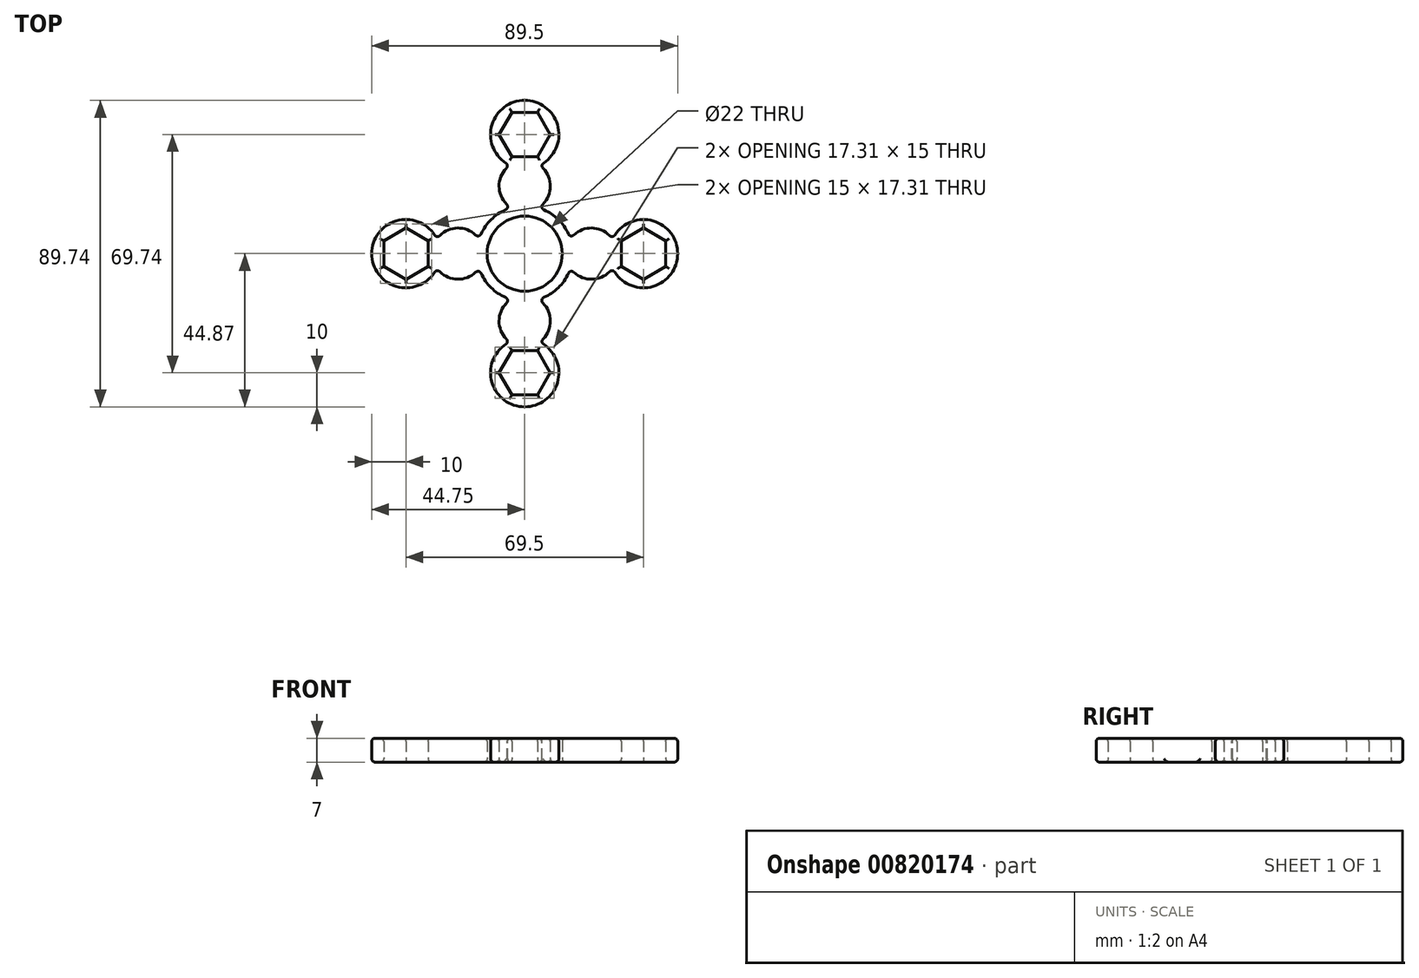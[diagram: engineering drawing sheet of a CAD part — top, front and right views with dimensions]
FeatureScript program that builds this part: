
annotation { "Feature Type Name" : "Feature", "Feature Type Description" : "" }
export const myFeature = defineFeature(function(context is Context, id is Id, definition is map)
    precondition{}
    {
        {
            var Q0;
            Q0=qCreatedBy(makeId("Top.planeOp"),FACE);
            var sketch = newSketch(context, id + "F0", { "sketchPlane" : qUnion([Q0])});
            skCircle(sketch, "E0", {"center": v(0, 0) * mm, "radius": 11 * mm});
            skCircle(sketch, "E1", {"center": v(0, 0) * mm, "radius": 14 * mm});
            skCircle(sketch, "E2", {"center": v(19.5, 0) * mm, "radius": 7.5 * mm});
            skCircle(sketch, "E3.MirrorC", {"center": v(-19.5, 0) * mm, "radius": 7.5 * mm});
            skCircle(sketch, "E4", {"center": v(0, 19.76) * mm, "radius": 7.5 * mm});
            skCircle(sketch, "E5.MirrorC", {"center": v(0, -19.76) * mm, "radius": 7.5 * mm});
            skCircle(sketch, "E6", {"center": v(34.75, 0) * mm, "radius": 10 * mm});
            skCircle(sketch, "E7.MirrorC", {"center": v(-34.75, 0) * mm, "radius": 10 * mm});
            skCircle(sketch, "E8", {"center": v(0, 34.87) * mm, "radius": 10 * mm});
            skCircle(sketch, "E9.MirrorC", {"center": v(0, -34.87) * mm, "radius": 10 * mm});
            skCircle(sketch, "E10.cCircle", {"center": v(34.75, 0) * mm, "radius": 6.5 * mm, "construction": true});
            skLineSegment(sketch, "E10.0", {"start": v(28.25, -3.75) * mm, "end": v(28.25, 3.75) * mm});
            skLineSegment(sketch, "E10.1", {"start": v(28.25, 3.75) * mm, "end": v(34.75, 7.5) * mm});
            skLineSegment(sketch, "E10.2", {"start": v(34.75, 7.5) * mm, "end": v(41.25, 3.75) * mm});
            skLineSegment(sketch, "E10.3", {"start": v(41.25, 3.75) * mm, "end": v(41.25, -3.75) * mm});
            skLineSegment(sketch, "E10.4", {"start": v(41.25, -3.75) * mm, "end": v(34.75, -7.5) * mm});
            skLineSegment(sketch, "E10.5", {"start": v(34.75, -7.5) * mm, "end": v(28.25, -3.75) * mm});
            skPoint(sketch, "E10.0.midPoint", {"position": v(28.25, 0) * mm});
            skCircle(sketch, "E11.cCircle", {"center": v(0, 34.87) * mm, "radius": 6.5 * mm, "construction": true});
            skLineSegment(sketch, "E11.0", {"start": v(3.75, 28.37) * mm, "end": v(-3.75, 28.37) * mm});
            skLineSegment(sketch, "E11.1", {"start": v(-3.75, 28.37) * mm, "end": v(-7.5, 34.87) * mm});
            skLineSegment(sketch, "E11.2", {"start": v(-7.5, 34.87) * mm, "end": v(-3.75, 41.37) * mm});
            skLineSegment(sketch, "E11.3", {"start": v(-3.75, 41.37) * mm, "end": v(3.75, 41.37) * mm});
            skLineSegment(sketch, "E11.4", {"start": v(3.75, 41.37) * mm, "end": v(7.5, 34.87) * mm});
            skLineSegment(sketch, "E11.5", {"start": v(7.5, 34.87) * mm, "end": v(3.75, 28.37) * mm});
            skPoint(sketch, "E11.0.midPoint", {"position": v(0, 28.37) * mm});
            skCircle(sketch, "E12.MirrorC", {"center": v(-34.75, 0) * mm, "radius": 6.5 * mm, "construction": true});
            skLineSegment(sketch, "E13.MirrorCS", {"start": v(-34.75, 7.5) * mm, "end": v(-41.25, 3.75) * mm});
            skLineSegment(sketch, "E14.MirrorCS", {"start": v(-41.25, -3.75) * mm, "end": v(-34.75, -7.5) * mm});
            skLineSegment(sketch, "E15.MirrorCS", {"start": v(-34.75, -7.5) * mm, "end": v(-28.25, -3.75) * mm});
            skLineSegment(sketch, "E16.MirrorCS", {"start": v(-28.25, -3.75) * mm, "end": v(-28.25, 3.75) * mm});
            skLineSegment(sketch, "E17.MirrorCS", {"start": v(-28.25, 3.75) * mm, "end": v(-34.75, 7.5) * mm});
            skLineSegment(sketch, "E18.MirrorCS", {"start": v(-41.25, 3.75) * mm, "end": v(-41.25, -3.75) * mm});
            skCircle(sketch, "E19.MirrorC", {"center": v(0, -34.87) * mm, "radius": 6.5 * mm, "construction": true});
            skLineSegment(sketch, "E20.MirrorCS", {"start": v(7.5, -34.87) * mm, "end": v(3.75, -28.37) * mm});
            skLineSegment(sketch, "E21.MirrorCS", {"start": v(3.75, -41.37) * mm, "end": v(7.5, -34.87) * mm});
            skLineSegment(sketch, "E22.MirrorCS", {"start": v(-3.75, -41.37) * mm, "end": v(3.75, -41.37) * mm});
            skLineSegment(sketch, "E23.MirrorCS", {"start": v(-7.5, -34.87) * mm, "end": v(-3.75, -41.37) * mm});
            skLineSegment(sketch, "E24.MirrorCS", {"start": v(-3.75, -28.37) * mm, "end": v(-7.5, -34.87) * mm});
            skLineSegment(sketch, "E25.MirrorCS", {"start": v(3.75, -28.37) * mm, "end": v(-3.75, -28.37) * mm});
            skSolve(sketch);
        }
        {
            var Q0;
            Q0 = qSketchRegion(id + "F0", true);
            extrude(context, id + "F1", {"entities" : qUnion([Q0]), "depth" : 7 * mm, "offsetDistance" : 25 * mm});
        }
        {
            var Q0;
            Q0=makeQuery(id+"F1.opExtrude","CAP_EDGE",EDGE,{"disambiguationData":[OSD([sQuery(id+"F0.wireOp",EDGE,"E0")])],"isStart":true});
            var Q1;
            {var subQ0=sQuery(id+"F0.wireOp",EDGE,"E1");Q1=makeQuery(id+"F1.opExtrude","CAP_EDGE",EDGE,{"disambiguationData":[OSD([subQ0]),TDD([makeQuery(id+"F0.imprint","IMPRINT",EDGE,{"disambiguationData":[TD([[makeQuery(id+"F0.imprint","INTERSECT",VERTEX,{"disambiguationData":[OD(1.0)],"derivedFrom":[subQ0,sQuery(id+"F0.wireOp",EDGE,"E5.MirrorC")]}),-1.0]])],"derivedFrom":subQ0})])],"isStart":true});}
            var Q2;
            {var subQ0=sQuery(id+"F0.wireOp",EDGE,"E1");Q2=makeQuery(id+"F1.opExtrude","CAP_EDGE",EDGE,{"disambiguationData":[OSD([subQ0]),TDD([makeQuery(id+"F0.imprint","IMPRINT",EDGE,{"disambiguationData":[TD([[makeQuery(id+"F0.imprint","INTERSECT",VERTEX,{"disambiguationData":[OD(1.0)],"derivedFrom":[subQ0,sQuery(id+"F0.wireOp",EDGE,"E3.MirrorC")]}),-1.0]])],"derivedFrom":subQ0})])],"isStart":true});}
            var Q3;
            {var subQ0=sQuery(id+"F0.wireOp",EDGE,"E1");Q3=makeQuery(id+"F1.opExtrude","CAP_EDGE",EDGE,{"disambiguationData":[OSD([subQ0]),TDD([makeQuery(id+"F0.imprint","IMPRINT",EDGE,{"disambiguationData":[TD([[makeQuery(id+"F0.imprint","INTERSECT",VERTEX,{"disambiguationData":[OD(1.0)],"derivedFrom":[subQ0,sQuery(id+"F0.wireOp",EDGE,"E4")]}),-1.0]])],"derivedFrom":subQ0})])],"isStart":true});}
            var Q4;
            {var subQ0=sQuery(id+"F0.wireOp",EDGE,"E1");Q4=makeQuery(id+"F1.opExtrude","CAP_EDGE",EDGE,{"disambiguationData":[OSD([subQ0]),TDD([makeQuery(id+"F0.imprint","IMPRINT",EDGE,{"disambiguationData":[TD([[makeQuery(id+"F0.imprint","INTERSECT",VERTEX,{"disambiguationData":[OD(0.0)],"derivedFrom":[subQ0,sQuery(id+"F0.wireOp",EDGE,"E4")]}),1.0]])],"derivedFrom":subQ0})])],"isStart":true});}
            var Q5;
            Q5=makeQuery(id+"F1.opExtrude","CAP_EDGE",EDGE,{"disambiguationData":[OSD([sQuery(id+"F0.wireOp",EDGE,"E13.MirrorCS")])],"isStart":true});
            var Q6;
            Q6=makeQuery(id+"F1.opExtrude","CAP_EDGE",EDGE,{"disambiguationData":[OSD([sQuery(id+"F0.wireOp",EDGE,"E17.MirrorCS")])],"isStart":true});
            var Q7;
            Q7=makeQuery(id+"F1.opExtrude","CAP_EDGE",EDGE,{"disambiguationData":[OSD([sQuery(id+"F0.wireOp",EDGE,"E16.MirrorCS")])],"isStart":true});
            var Q8;
            Q8=makeQuery(id+"F1.opExtrude","CAP_EDGE",EDGE,{"disambiguationData":[OSD([sQuery(id+"F0.wireOp",EDGE,"E15.MirrorCS")])],"isStart":true});
            var Q9;
            Q9=makeQuery(id+"F1.opExtrude","CAP_EDGE",EDGE,{"disambiguationData":[OSD([sQuery(id+"F0.wireOp",EDGE,"E14.MirrorCS")])],"isStart":true});
            var Q10;
            Q10=makeQuery(id+"F1.opExtrude","CAP_EDGE",EDGE,{"disambiguationData":[OSD([sQuery(id+"F0.wireOp",EDGE,"E18.MirrorCS")])],"isStart":true});
            var Q11;
            Q11=makeQuery(id+"F1.opExtrude","CAP_EDGE",EDGE,{"disambiguationData":[OSD([sQuery(id+"F0.wireOp",EDGE,"E10.4")])],"isStart":true});
            var Q12;
            Q12=makeQuery(id+"F1.opExtrude","CAP_EDGE",EDGE,{"disambiguationData":[OSD([sQuery(id+"F0.wireOp",EDGE,"E10.5")])],"isStart":true});
            var Q13;
            Q13=makeQuery(id+"F1.opExtrude","CAP_EDGE",EDGE,{"disambiguationData":[OSD([sQuery(id+"F0.wireOp",EDGE,"E10.0")])],"isStart":true});
            var Q14;
            Q14=makeQuery(id+"F1.opExtrude","CAP_EDGE",EDGE,{"disambiguationData":[OSD([sQuery(id+"F0.wireOp",EDGE,"E10.1")])],"isStart":true});
            var Q15;
            Q15=makeQuery(id+"F1.opExtrude","CAP_EDGE",EDGE,{"disambiguationData":[OSD([sQuery(id+"F0.wireOp",EDGE,"E10.2")])],"isStart":true});
            var Q16;
            Q16=makeQuery(id+"F1.opExtrude","CAP_EDGE",EDGE,{"disambiguationData":[OSD([sQuery(id+"F0.wireOp",EDGE,"E10.3")])],"isStart":true});
            var Q17;
            Q17=makeQuery(id+"F1.opExtrude","CAP_EDGE",EDGE,{"disambiguationData":[OSD([sQuery(id+"F0.wireOp",EDGE,"E25.MirrorCS")])],"isStart":true});
            var Q18;
            Q18=makeQuery(id+"F1.opExtrude","CAP_EDGE",EDGE,{"disambiguationData":[OSD([sQuery(id+"F0.wireOp",EDGE,"E24.MirrorCS")])],"isStart":true});
            var Q19;
            Q19=makeQuery(id+"F1.opExtrude","CAP_EDGE",EDGE,{"disambiguationData":[OSD([sQuery(id+"F0.wireOp",EDGE,"E23.MirrorCS")])],"isStart":true});
            var Q20;
            Q20=makeQuery(id+"F1.opExtrude","CAP_EDGE",EDGE,{"disambiguationData":[OSD([sQuery(id+"F0.wireOp",EDGE,"E22.MirrorCS")])],"isStart":true});
            var Q21;
            Q21=makeQuery(id+"F1.opExtrude","CAP_EDGE",EDGE,{"disambiguationData":[OSD([sQuery(id+"F0.wireOp",EDGE,"E21.MirrorCS")])],"isStart":true});
            var Q22;
            Q22=makeQuery(id+"F1.opExtrude","CAP_EDGE",EDGE,{"disambiguationData":[OSD([sQuery(id+"F0.wireOp",EDGE,"E20.MirrorCS")])],"isStart":true});
            var Q23;
            Q23=makeQuery(id+"F1.opExtrude","CAP_EDGE",EDGE,{"disambiguationData":[OSD([sQuery(id+"F0.wireOp",EDGE,"E11.1")])],"isStart":true});
            var Q24;
            Q24=makeQuery(id+"F1.opExtrude","CAP_EDGE",EDGE,{"disambiguationData":[OSD([sQuery(id+"F0.wireOp",EDGE,"E11.2")])],"isStart":true});
            var Q25;
            Q25=makeQuery(id+"F1.opExtrude","CAP_EDGE",EDGE,{"disambiguationData":[OSD([sQuery(id+"F0.wireOp",EDGE,"E11.3")])],"isStart":true});
            var Q26;
            Q26=makeQuery(id+"F1.opExtrude","CAP_EDGE",EDGE,{"disambiguationData":[OSD([sQuery(id+"F0.wireOp",EDGE,"E11.4")])],"isStart":true});
            var Q27;
            Q27=makeQuery(id+"F1.opExtrude","CAP_EDGE",EDGE,{"disambiguationData":[OSD([sQuery(id+"F0.wireOp",EDGE,"E11.5")])],"isStart":true});
            var Q28;
            Q28=makeQuery(id+"F1.opExtrude","CAP_EDGE",EDGE,{"disambiguationData":[OSD([sQuery(id+"F0.wireOp",EDGE,"E11.0")])],"isStart":true});
            var Q29;
            {var subQ0=sQuery(id+"F0.wireOp",EDGE,"E4");Q29=makeQuery(id+"F1.opExtrude","SWEPT_FACE",FACE,{"disambiguationData":[OSD([subQ0]),TDD([makeQuery(id+"F0.imprint","IMPRINT",EDGE,{"disambiguationData":[TD([[makeQuery(id+"F0.imprint","INTERSECT",VERTEX,{"disambiguationData":[OD(1.0)],"derivedFrom":[sQuery(id+"F0.wireOp",EDGE,"E1"),subQ0]}),1.0]])],"derivedFrom":subQ0})])]});}
            var Q30;
            Q30=makeQuery(id+"F1.opExtrude","SWEPT_FACE",FACE,{"disambiguationData":[OSD([sQuery(id+"F0.wireOp",EDGE,"E8")])]});
            var Q31;
            {var subQ0=sQuery(id+"F0.wireOp",EDGE,"E4");Q31=makeQuery(id+"F1.opExtrude","SWEPT_FACE",FACE,{"disambiguationData":[OSD([subQ0]),TDD([makeQuery(id+"F0.imprint","IMPRINT",EDGE,{"disambiguationData":[TD([[makeQuery(id+"F0.imprint","INTERSECT",VERTEX,{"disambiguationData":[OD(0.0)],"derivedFrom":[sQuery(id+"F0.wireOp",EDGE,"E1"),subQ0]}),-1.0]])],"derivedFrom":subQ0})])]});}
            var Q32;
            {var subQ0=sQuery(id+"F0.wireOp",EDGE,"E1");Q32=makeQuery(id+"F1.opExtrude","SWEPT_FACE",FACE,{"disambiguationData":[OSD([subQ0]),TDD([makeQuery(id+"F0.imprint","IMPRINT",EDGE,{"disambiguationData":[TD([[makeQuery(id+"F0.imprint","INTERSECT",VERTEX,{"disambiguationData":[OD(0.0)],"derivedFrom":[subQ0,sQuery(id+"F0.wireOp",EDGE,"E4")]}),1.0]])],"derivedFrom":subQ0})])]});}
            var Q33;
            {var subQ0=sQuery(id+"F0.wireOp",EDGE,"E2");Q33=makeQuery(id+"F1.opExtrude","SWEPT_FACE",FACE,{"disambiguationData":[OSD([subQ0]),TDD([makeQuery(id+"F0.imprint","IMPRINT",EDGE,{"disambiguationData":[TD([[makeQuery(id+"F0.imprint","INTERSECT",VERTEX,{"disambiguationData":[OD(0.0)],"derivedFrom":[sQuery(id+"F0.wireOp",EDGE,"E1"),subQ0]}),1.0]])],"derivedFrom":subQ0})])]});}
            var Q34;
            Q34=makeQuery(id+"F1.opExtrude","SWEPT_FACE",FACE,{"disambiguationData":[OSD([sQuery(id+"F0.wireOp",EDGE,"E6")])]});
            var Q35;
            {var subQ0=sQuery(id+"F0.wireOp",EDGE,"E2");Q35=makeQuery(id+"F1.opExtrude","SWEPT_FACE",FACE,{"disambiguationData":[OSD([subQ0]),TDD([makeQuery(id+"F0.imprint","IMPRINT",EDGE,{"disambiguationData":[TD([[makeQuery(id+"F0.imprint","INTERSECT",VERTEX,{"disambiguationData":[OD(1.0)],"derivedFrom":[sQuery(id+"F0.wireOp",EDGE,"E1"),subQ0]}),-1.0]])],"derivedFrom":subQ0})])]});}
            var Q36;
            {var subQ0=sQuery(id+"F0.wireOp",EDGE,"E1");Q36=makeQuery(id+"F1.opExtrude","SWEPT_FACE",FACE,{"disambiguationData":[OSD([subQ0]),TDD([makeQuery(id+"F0.imprint","IMPRINT",EDGE,{"disambiguationData":[TD([[makeQuery(id+"F0.imprint","INTERSECT",VERTEX,{"disambiguationData":[OD(1.0)],"derivedFrom":[subQ0,sQuery(id+"F0.wireOp",EDGE,"E5.MirrorC")]}),-1.0]])],"derivedFrom":subQ0})])]});}
            var Q37;
            {var subQ0=sQuery(id+"F0.wireOp",EDGE,"E5.MirrorC");Q37=makeQuery(id+"F1.opExtrude","SWEPT_FACE",FACE,{"disambiguationData":[OSD([subQ0]),TDD([makeQuery(id+"F0.imprint","IMPRINT",EDGE,{"disambiguationData":[TD([[makeQuery(id+"F0.imprint","INTERSECT",VERTEX,{"disambiguationData":[OD(1.0)],"derivedFrom":[sQuery(id+"F0.wireOp",EDGE,"E1"),subQ0]}),-1.0]])],"derivedFrom":subQ0})])]});}
            var Q38;
            Q38=makeQuery(id+"F1.opExtrude","SWEPT_FACE",FACE,{"disambiguationData":[OSD([sQuery(id+"F0.wireOp",EDGE,"E9.MirrorC")])]});
            var Q39;
            {var subQ0=sQuery(id+"F0.wireOp",EDGE,"E1");Q39=makeQuery(id+"F1.opExtrude","SWEPT_FACE",FACE,{"disambiguationData":[OSD([subQ0]),TDD([makeQuery(id+"F0.imprint","IMPRINT",EDGE,{"disambiguationData":[TD([[makeQuery(id+"F0.imprint","INTERSECT",VERTEX,{"disambiguationData":[OD(1.0)],"derivedFrom":[subQ0,sQuery(id+"F0.wireOp",EDGE,"E3.MirrorC")]}),-1.0]])],"derivedFrom":subQ0})])]});}
            var Q40;
            {var subQ0=sQuery(id+"F0.wireOp",EDGE,"E5.MirrorC");Q40=makeQuery(id+"F1.opExtrude","SWEPT_FACE",FACE,{"disambiguationData":[OSD([subQ0]),TDD([makeQuery(id+"F0.imprint","IMPRINT",EDGE,{"disambiguationData":[TD([[makeQuery(id+"F0.imprint","INTERSECT",VERTEX,{"disambiguationData":[OD(0.0)],"derivedFrom":[sQuery(id+"F0.wireOp",EDGE,"E1"),subQ0]}),1.0]])],"derivedFrom":subQ0})])]});}
            var Q41;
            {var subQ0=sQuery(id+"F0.wireOp",EDGE,"E3.MirrorC");Q41=makeQuery(id+"F1.opExtrude","SWEPT_FACE",FACE,{"disambiguationData":[OSD([subQ0]),TDD([makeQuery(id+"F0.imprint","IMPRINT",EDGE,{"disambiguationData":[TD([[makeQuery(id+"F0.imprint","INTERSECT",VERTEX,{"disambiguationData":[OD(1.0)],"derivedFrom":[sQuery(id+"F0.wireOp",EDGE,"E1"),subQ0]}),1.0]])],"derivedFrom":subQ0})])]});}
            var Q42;
            Q42=makeQuery(id+"F1.opExtrude","SWEPT_FACE",FACE,{"disambiguationData":[OSD([sQuery(id+"F0.wireOp",EDGE,"E7.MirrorC")])]});
            var Q43;
            {var subQ0=sQuery(id+"F0.wireOp",EDGE,"E1");Q43=makeQuery(id+"F1.opExtrude","SWEPT_FACE",FACE,{"disambiguationData":[OSD([subQ0]),TDD([makeQuery(id+"F0.imprint","IMPRINT",EDGE,{"disambiguationData":[TD([[makeQuery(id+"F0.imprint","INTERSECT",VERTEX,{"disambiguationData":[OD(1.0)],"derivedFrom":[subQ0,sQuery(id+"F0.wireOp",EDGE,"E4")]}),-1.0]])],"derivedFrom":subQ0})])]});}
            var Q44;
            {var subQ0=sQuery(id+"F0.wireOp",EDGE,"E3.MirrorC");Q44=makeQuery(id+"F1.opExtrude","SWEPT_FACE",FACE,{"disambiguationData":[OSD([subQ0]),TDD([makeQuery(id+"F0.imprint","IMPRINT",EDGE,{"disambiguationData":[TD([[makeQuery(id+"F0.imprint","INTERSECT",VERTEX,{"disambiguationData":[OD(0.0)],"derivedFrom":[sQuery(id+"F0.wireOp",EDGE,"E1"),subQ0]}),-1.0]])],"derivedFrom":subQ0})])]});}
            var Q45;
            Q45=makeQuery(id+"F1.opExtrude","CAP_EDGE",EDGE,{"disambiguationData":[OSD([sQuery(id+"F0.wireOp",EDGE,"E14.MirrorCS")])],"isStart":false});
            var Q46;
            Q46=makeQuery(id+"F1.opExtrude","CAP_EDGE",EDGE,{"disambiguationData":[OSD([sQuery(id+"F0.wireOp",EDGE,"E13.MirrorCS")])],"isStart":false});
            var Q47;
            Q47=makeQuery(id+"F1.opExtrude","CAP_EDGE",EDGE,{"disambiguationData":[OSD([sQuery(id+"F0.wireOp",EDGE,"E17.MirrorCS")])],"isStart":false});
            var Q48;
            Q48=makeQuery(id+"F1.opExtrude","CAP_EDGE",EDGE,{"disambiguationData":[OSD([sQuery(id+"F0.wireOp",EDGE,"E16.MirrorCS")])],"isStart":false});
            var Q49;
            Q49=makeQuery(id+"F1.opExtrude","CAP_EDGE",EDGE,{"disambiguationData":[OSD([sQuery(id+"F0.wireOp",EDGE,"E15.MirrorCS")])],"isStart":false});
            var Q50;
            Q50=makeQuery(id+"F1.opExtrude","CAP_EDGE",EDGE,{"disambiguationData":[OSD([sQuery(id+"F0.wireOp",EDGE,"E18.MirrorCS")])],"isStart":false});
            var Q51;
            Q51=makeQuery(id+"F1.opExtrude","CAP_FACE",FACE,{"disambiguationData":[OSD([sQuery(id+"F0.wireOp",EDGE,"E0"),sQuery(id+"F0.wireOp",EDGE,"E1"),sQuery(id+"F0.wireOp",EDGE,"E2"),sQuery(id+"F0.wireOp",EDGE,"E3.MirrorC"),sQuery(id+"F0.wireOp",EDGE,"E4"),sQuery(id+"F0.wireOp",EDGE,"E5.MirrorC"),sQuery(id+"F0.wireOp",EDGE,"E6"),sQuery(id+"F0.wireOp",EDGE,"E7.MirrorC"),sQuery(id+"F0.wireOp",EDGE,"E8"),sQuery(id+"F0.wireOp",EDGE,"E9.MirrorC"),sQuery(id+"F0.wireOp",EDGE,"E10.0"),sQuery(id+"F0.wireOp",EDGE,"E10.1"),sQuery(id+"F0.wireOp",EDGE,"E10.2"),sQuery(id+"F0.wireOp",EDGE,"E10.3"),sQuery(id+"F0.wireOp",EDGE,"E10.4"),sQuery(id+"F0.wireOp",EDGE,"E10.5"),sQuery(id+"F0.wireOp",EDGE,"E11.0"),sQuery(id+"F0.wireOp",EDGE,"E11.1"),sQuery(id+"F0.wireOp",EDGE,"E11.2"),sQuery(id+"F0.wireOp",EDGE,"E11.3"),sQuery(id+"F0.wireOp",EDGE,"E11.4"),sQuery(id+"F0.wireOp",EDGE,"E11.5"),sQuery(id+"F0.wireOp",EDGE,"E13.MirrorCS"),sQuery(id+"F0.wireOp",EDGE,"E14.MirrorCS"),sQuery(id+"F0.wireOp",EDGE,"E15.MirrorCS"),sQuery(id+"F0.wireOp",EDGE,"E16.MirrorCS"),sQuery(id+"F0.wireOp",EDGE,"E17.MirrorCS"),sQuery(id+"F0.wireOp",EDGE,"E18.MirrorCS"),sQuery(id+"F0.wireOp",EDGE,"E20.MirrorCS"),sQuery(id+"F0.wireOp",EDGE,"E21.MirrorCS"),sQuery(id+"F0.wireOp",EDGE,"E22.MirrorCS"),sQuery(id+"F0.wireOp",EDGE,"E23.MirrorCS"),sQuery(id+"F0.wireOp",EDGE,"E24.MirrorCS"),sQuery(id+"F0.wireOp",EDGE,"E25.MirrorCS")])],"isStart":false});
            fillet(context, id + "F2", {"entities" : qUnion([Q0, Q1, Q2, Q3, Q4, Q5, Q6, Q7, Q8, Q9, Q10, Q11, Q12, Q13, Q14, Q15, Q16, Q17, Q18, Q19, Q20, Q21, Q22, Q23, Q24, Q25, Q26, Q27, Q28, Q29, Q30, Q31, Q32, Q33, Q34, Q35, Q36, Q37, Q38, Q39, Q40, Q41, Q42, Q43, Q44, Q45, Q46, Q47, Q48, Q49, Q50, Q51]), "radius" : 1 * mm, "tangentPropagation" : true, "allowEdgeOverflow" : false});
        }
    });
